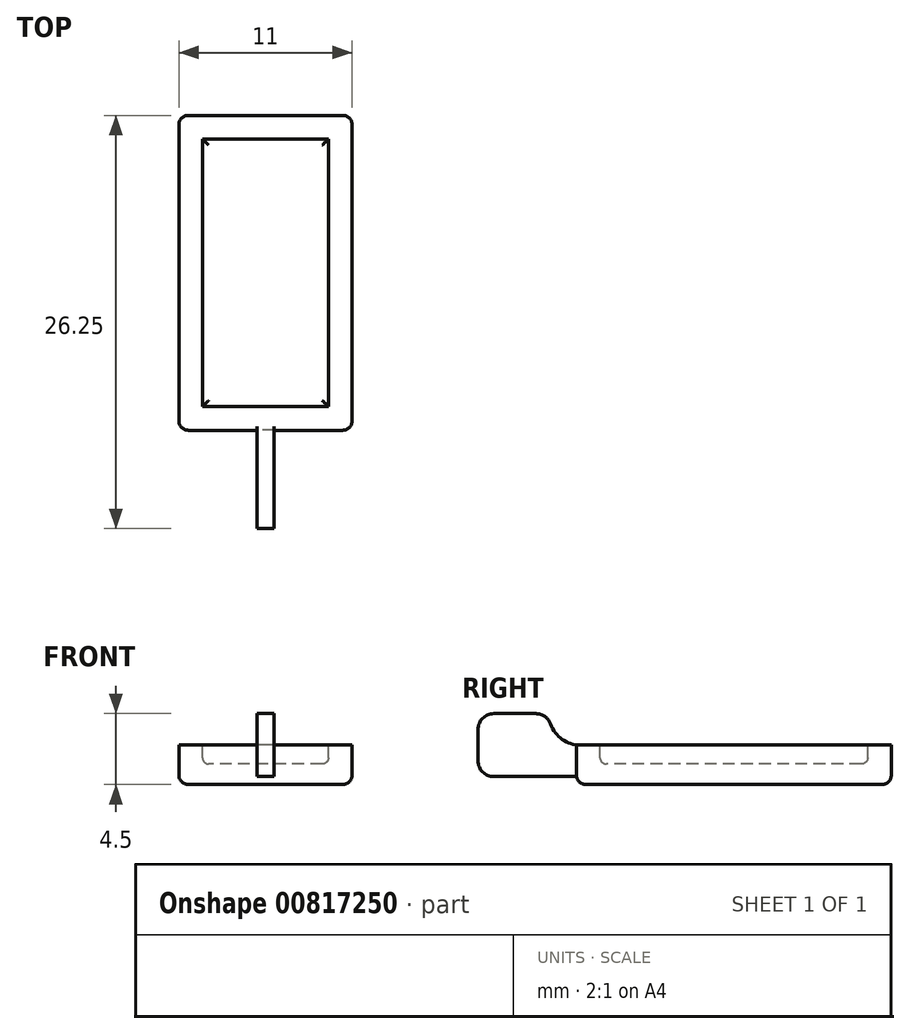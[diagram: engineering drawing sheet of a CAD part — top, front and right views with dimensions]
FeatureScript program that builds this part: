
annotation { "Feature Type Name" : "Feature", "Feature Type Description" : "" }
export const myFeature = defineFeature(function(context is Context, id is Id, definition is map)
    precondition{}
    {
        {
            var Q0;
            Q0=qCreatedBy(makeId("Top.planeOp"),FACE);
            var sketch = newSketch(context, id + "F0", { "sketchPlane" : qUnion([Q0])});
            skLineSegment(sketch, "E0.bottom", {"start": v(5.5, 10) * mm, "end": v(-5.5, 10) * mm});
            skLineSegment(sketch, "E0.top", {"start": v(5.5, -10) * mm, "end": v(-5.5, -10) * mm});
            skLineSegment(sketch, "E0.left", {"start": v(5.5, 10) * mm, "end": v(5.5, -10) * mm});
            skLineSegment(sketch, "E0.right", {"start": v(-5.5, 10) * mm, "end": v(-5.5, -10) * mm});
            skPoint(sketch, "E0.middle", {"position": v(0, 0) * mm});
            skSolve(sketch);
        }
        {
            var Q0;
            Q0=qSketchRegion(id+"F0",true);
            extrude(context, id + "F1", {"entities" : qUnion([Q0]), "oppositeDirection" : true, "depth" : 2.5 * mm, "offsetDistance" : 25 * mm});
        }
        {
            var Q0;
            Q0=makeQuery(id+"FCpzT19OhP4sAUk_1.boolean.opBoolean","MERGE",FACE,{"derivedFrom":[makeQuery(id+"F1.opExtrude","CAP_FACE",FACE,{"disambiguationData":[OSD([sQuery(id+"F0.wireOp",EDGE,"E0.bottom"),sQuery(id+"F0.wireOp",EDGE,"E0.top"),sQuery(id+"F0.wireOp",EDGE,"E0.left"),sQuery(id+"F0.wireOp",EDGE,"E0.right")])],"isStart":true}),makeQuery(id+"FCpzT19OhP4sAUk_1.opExtrude","CAP_FACE",FACE,{"disambiguationData":[OSD([sQuery(id+"FikGxf4bu9mYxne_1.wireOp",EDGE,"8oJKbysR-RPwh-InYj-CVRJ-1ywRJHMkg91W.bottom"),sQuery(id+"FikGxf4bu9mYxne_1.wireOp",EDGE,"8oJKbysR-RPwh-InYj-CVRJ-1ywRJHMkg91W.top"),sQuery(id+"FikGxf4bu9mYxne_1.wireOp",EDGE,"8oJKbysR-RPwh-InYj-CVRJ-1ywRJHMkg91W.left"),sQuery(id+"FikGxf4bu9mYxne_1.wireOp",EDGE,"8oJKbysR-RPwh-InYj-CVRJ-1ywRJHMkg91W.right")])],"isStart":true})]});
            var sketch = newSketch(context, id + "F2", { "sketchPlane" : qUnion([Q0])});
            skLineSegment(sketch, "E1.bottom", {"start": v(4, 8.5) * mm, "end": v(-4, 8.5) * mm});
            skLineSegment(sketch, "E1.top", {"start": v(4, -8.5) * mm, "end": v(-4, -8.5) * mm});
            skLineSegment(sketch, "E1.left", {"start": v(4, 8.5) * mm, "end": v(4, -8.5) * mm});
            skLineSegment(sketch, "E1.right", {"start": v(-4, 8.5) * mm, "end": v(-4, -8.5) * mm});
            skPoint(sketch, "E1.middle", {"position": v(0, 0) * mm});
            skSolve(sketch);
        }
        {
            var Q0;
            Q0=qSketchRegion(id+"F2",true);
            extrude(context, id + "F3", {"entities" : qUnion([Q0]), "operationType" : NewBodyOperationType.REMOVE, "oppositeDirection" : true, "depth" : 1.2 * mm, "offsetDistance" : 25 * mm});
        }
        {
            var Q0;
            Q0=makeQuery(id+"F3.boolean.opBoolean","COPY",FACE,{"derivedFrom":makeQuery(id+"F3.opExtrude","CAP_FACE",FACE,{"disambiguationData":[OSD([sQuery(id+"F2.wireOp",EDGE,"E1.bottom"),sQuery(id+"F2.wireOp",EDGE,"E1.top"),sQuery(id+"F2.wireOp",EDGE,"E1.left"),sQuery(id+"F2.wireOp",EDGE,"E1.right")])],"isStart":false})});
            fillet(context, id + "F4", {"entities" : qUnion([Q0]), "radius" : .4 * mm, "tangentPropagation" : true, "allowEdgeOverflow" : false});
        }
        {
            var Q0;
            Q0=makeQuery(id+"F1.opExtrude","CAP_FACE",FACE,{"disambiguationData":[OSD([sQuery(id+"F0.wireOp",EDGE,"E0.bottom"),sQuery(id+"F0.wireOp",EDGE,"E0.top"),sQuery(id+"F0.wireOp",EDGE,"E0.left"),sQuery(id+"F0.wireOp",EDGE,"E0.right")])],"isStart":false});
            var Q1;
            Q1=makeQuery(id+"F1.opExtrude","SWEPT_EDGE",EDGE,{"disambiguationData":[OSD([sQuery(id+"F0.wireOp",EDGE,"E0.top"),sQuery(id+"F0.wireOp",EDGE,"E0.left")])]});
            var Q2;
            Q2=makeQuery(id+"F1.opExtrude","SWEPT_EDGE",EDGE,{"disambiguationData":[OSD([sQuery(id+"F0.wireOp",EDGE,"E0.top"),sQuery(id+"F0.wireOp",EDGE,"E0.right")])]});
            var Q3;
            Q3=makeQuery(id+"F1.opExtrude","SWEPT_EDGE",EDGE,{"disambiguationData":[OSD([sQuery(id+"F0.wireOp",EDGE,"E0.bottom"),sQuery(id+"F0.wireOp",EDGE,"E0.right")])]});
            var Q4;
            Q4=makeQuery(id+"F1.opExtrude","SWEPT_EDGE",EDGE,{"disambiguationData":[OSD([sQuery(id+"F0.wireOp",EDGE,"E0.bottom"),sQuery(id+"F0.wireOp",EDGE,"E0.left")])]});
            fillet(context, id + "F5", {"entities" : qUnion([Q0, Q1, Q2, Q3, Q4]), "radius" : .6 * mm, "tangentPropagation" : true, "allowEdgeOverflow" : false});
        }
        {
            var Q0;
            Q0=makeQuery(id+"FCpzT19OhP4sAUk_1.boolean.opBoolean","MERGE",FACE,{"derivedFrom":[makeQuery(id+"F1.opExtrude","CAP_FACE",FACE,{"disambiguationData":[OSD([sQuery(id+"F0.wireOp",EDGE,"E0.bottom"),sQuery(id+"F0.wireOp",EDGE,"E0.top"),sQuery(id+"F0.wireOp",EDGE,"E0.left"),sQuery(id+"F0.wireOp",EDGE,"E0.right")])],"isStart":true}),makeQuery(id+"FCpzT19OhP4sAUk_1.opExtrude","CAP_FACE",FACE,{"disambiguationData":[OSD([sQuery(id+"FikGxf4bu9mYxne_1.wireOp",EDGE,"8oJKbysR-RPwh-InYj-CVRJ-1ywRJHMkg91W.bottom"),sQuery(id+"FikGxf4bu9mYxne_1.wireOp",EDGE,"8oJKbysR-RPwh-InYj-CVRJ-1ywRJHMkg91W.top"),sQuery(id+"FikGxf4bu9mYxne_1.wireOp",EDGE,"8oJKbysR-RPwh-InYj-CVRJ-1ywRJHMkg91W.left"),sQuery(id+"FikGxf4bu9mYxne_1.wireOp",EDGE,"8oJKbysR-RPwh-InYj-CVRJ-1ywRJHMkg91W.right")])],"isStart":true})]});
            var sketch = newSketch(context, id + "F6", { "sketchPlane" : qUnion([Q0])});
            skLineSegment(sketch, "E2.bottom", {"start": v(0.55, -9.75) * mm, "end": v(-0.55, -9.75) * mm});
            skLineSegment(sketch, "E2.top", {"start": v(0.55, -16.25) * mm, "end": v(-0.55, -16.25) * mm});
            skLineSegment(sketch, "E2.left", {"start": v(0.55, -9.75) * mm, "end": v(0.55, -16.25) * mm});
            skLineSegment(sketch, "E2.right", {"start": v(-0.55, -9.75) * mm, "end": v(-0.55, -16.25) * mm});
            skPoint(sketch, "E2.middle", {"position": v(0, -13) * mm});
            skSolve(sketch);
        }
        {
            var Q0;
            Q0=qSketchRegion(id+"F6",true);
            extrude(context, id + "F7", {"entities" : qUnion([Q0]), "operationType" : NewBodyOperationType.ADD, "endBound" : BoundingType.SYMMETRIC, "oppositeDirection" : true, "depth" : 4 * mm, "offsetDistance" : 25 * mm});
        }
        {
            var Q0;
            Q0=makeQuery(id+"F7.opExtrude","SWEPT_FACE",FACE,{"disambiguationData":[OSD([sQuery(id+"F6.wireOp",EDGE,"E2.left")])]});
            var sketch = newSketch(context, id + "F8", { "sketchPlane" : qUnion([Q0])});
            skCircle(sketch, "E3", {"center": v(-9.75, 2) * mm, "radius": 2 * mm});
            skSolve(sketch);
        }
        {
            var Q0;
            Q0 = qSketchRegion(id + "F8", true);
            extrude(context, id + "F9", {"entities" : qUnion([Q0]), "operationType" : NewBodyOperationType.REMOVE, "oppositeDirection" : true, "depth" : 25 * mm, "offsetDistance" : 25 * mm});
        }
        {
            var Q0;
            Q0=makeQuery(id+"F7.opExtrude","CAP_EDGE",EDGE,{"disambiguationData":[OSD([sQuery(id+"F6.wireOp",EDGE,"E2.top")])],"isStart":true});
            var Q1;
            Q1=makeQuery(id+"F7.opExtrude","CAP_EDGE",EDGE,{"disambiguationData":[OSD([sQuery(id+"F6.wireOp",EDGE,"E2.top")])],"isStart":false});
            var Q2;
            Q2=makeQuery(id+"F9.boolean.opBoolean","INTERSECT",EDGE,{"derivedFrom":[makeQuery(id+"F7.opExtrude","CAP_FACE",FACE,{"disambiguationData":[OSD([sQuery(id+"F6.wireOp",EDGE,"E2.bottom"),sQuery(id+"F6.wireOp",EDGE,"E2.top"),sQuery(id+"F6.wireOp",EDGE,"E2.left"),sQuery(id+"F6.wireOp",EDGE,"E2.right")])],"isStart":true}),makeQuery(id+"F9.opExtrude","SWEPT_FACE",FACE,{"disambiguationData":[OSD([sQuery(id+"F8.wireOp",EDGE,"E3")])]})]});
            fillet(context, id + "F10", {"entities" : qUnion([Q0, Q1, Q2]), "radius" : 1 * mm, "tangentPropagation" : true, "allowEdgeOverflow" : false});
        }
    });
